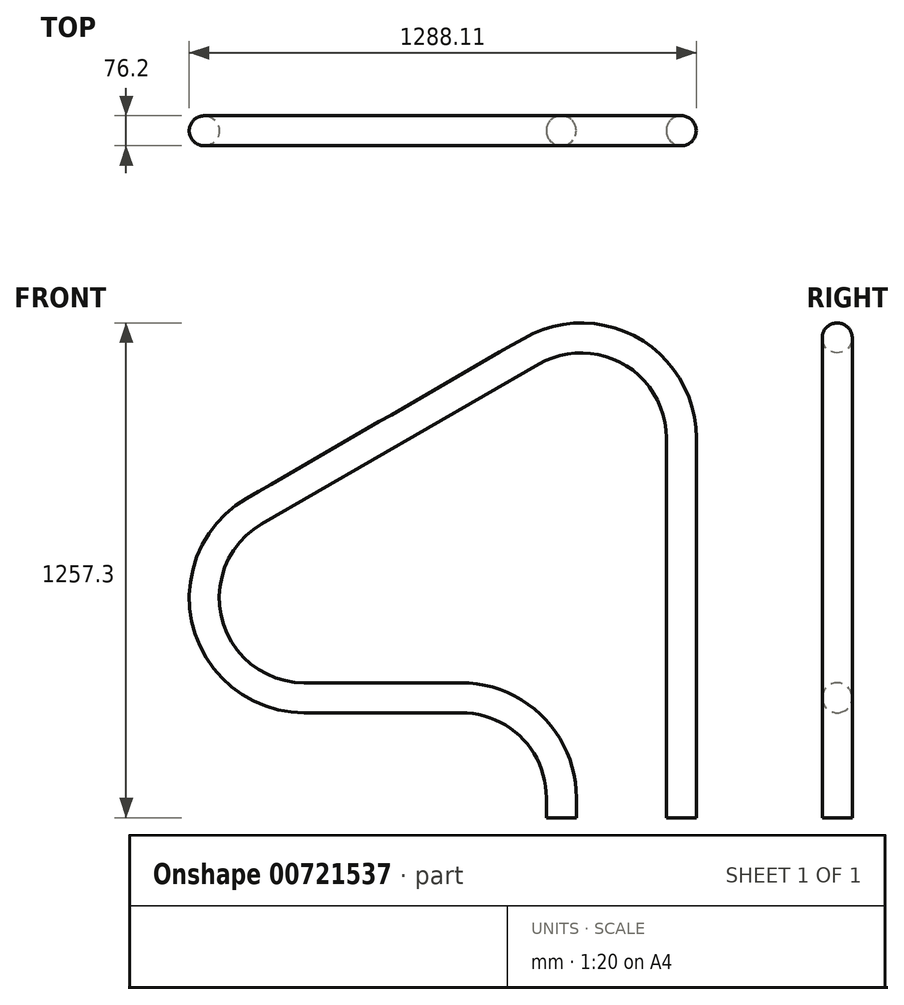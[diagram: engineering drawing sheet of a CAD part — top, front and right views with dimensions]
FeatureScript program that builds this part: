
annotation { "Feature Type Name" : "Feature", "Feature Type Description" : "" }
export const myFeature = defineFeature(function(context is Context, id is Id, definition is map)
    precondition{}
    {
        {
            var Q0;
            Q0=qCreatedBy(makeId("Front.planeOp"),FACE);
            var sketch = newSketch(context, id + "F0", { "sketchPlane" : qUnion([Q0])});
            skLineSegment(sketch, "E0", {"start": v(0, 0) * mm, "end": v(0, 965.2) * mm});
            skLineSegment(sketch, "E1", {"start": v(-381, 1185.17) * mm, "end": v(-1084.9, 778.77) * mm});
            skLineSegment(sketch, "E2", {"start": v(-957.9, 304.8) * mm, "end": v(-558.8, 304.8) * mm});
            skLineSegment(sketch, "E3", {"start": v(-304.8, 50.8) * mm, "end": v(-304.8, 0) * mm});
            skPoint(sketch, "E4.visualSharp", {"position": v(0, 1405.14) * mm});
            skArc(sketch, "E4.filletArc", {"start": v(0, 965.2) * mm, "mid": v(-127, 1185.17) * mm, "end": v(-381, 1185.17) * mm});
            skPoint(sketch, "E5.visualSharp", {"position": v(-1905.85, 304.8) * mm});
            skArc(sketch, "E5.filletArc", {"start": v(-1084.9, 778.77) * mm, "mid": v(-1203.25, 493.06) * mm, "end": v(-957.9, 304.8) * mm});
            skPoint(sketch, "E6.visualSharp", {"position": v(-304.8, 304.8) * mm});
            skArc(sketch, "E6.filletArc", {"start": v(-304.8, 50.8) * mm, "mid": v(-379.2, 230.4) * mm, "end": v(-558.8, 304.8) * mm});
            skLineSegment(sketch, "E7", {"start": v(-476.61, 1219.2) * mm, "end": v(99.39, 1219.2) * mm, "construction": true});
            skSolve(sketch);
        }
        {
            var Q0;
            Q0=sQuery(id+"F0.wireOp",VERTEX,"E0.start");
            var Q1;
            Q1=sQuery(id+"F0.wireOp",EDGE,"E0");
            cPlane(context, id + "F1", {"entities" : qUnion([Q0, Q1]), "cplaneType" : CPlaneType.LINE_POINT, "offset" : 25.4 * mm, "width" : 152.4 * mm, "height" : 152.4 * mm});
        }
        {
            var Q0;
            Q0=qCreatedBy(id+"F1.planeOp",FACE);
            var sketch = newSketch(context, id + "F2", { "sketchPlane" : qUnion([Q0])});
            skCircle(sketch, "E8", {"center": v(0, 0) * mm, "radius": 38.1 * mm});
            skSolve(sketch);
        }
        {
            var Q0;
            Q0=makeQuery(id+"F2.imprint","IMPRINT",FACE,{"disambiguationData":[TD([[makeQuery(id+"F2.imprint","IMPRINT",EDGE,{"derivedFrom":sQuery(id+"F2.wireOp",EDGE,"E8")}),1.0]])]});
            var Q1;
            Q1 = qConstructionFilter(qBodyType(qCreatedBy(id + "F0" ,EDGE), BodyType.WIRE), ConstructionObject.NO);
            sweep(context, id + "F3", {"profiles" : qUnion([Q0]), "path" : qUnion([Q1])});
        }
    });
